# Revit family: IS_iLifeA_T4709_BIM_GB
name_source: partatom
category: Plumbing Fixtures
units: mm (PartAtom-declared; Revit-internal decimal feet)

## family parameters
Always vertical = No
Cut with Voids When Loaded = No
OmniClass Number = 23.45.05.14.14
OmniClass Title = Sinks/Lavatories
Part Type = Normal
Room Calculation Point = No
Round Connector Dimension = Use Diameter
Shared = No
Work Plane-Based = No

## types (1)
- T470901 - Ideal Standard i.life A  handrinse 35 cm with left hand taphole, white
    Accessories = https://www.idealstandard.co.uk
    AreaUnits = millimetres
    AssetType = fixed
    BIMObjectName = IS_IdealStandard_Wall-hunghandrinsebasins_i.lifeA_T4709
    BIMobject category = Wash Basins
    BIMobject category code = wash-basins
    BIMobject main category = Sanitary
    BIMobject main category code = sanitary
    BarCode = 8014140486862
    Brand = Ideal Standard
    Brand url = http://www.idealstandard.co.uk
    Color = White
    ConnectionType = Plumbing
    CurrencyUnit = £
    CurrentRevision = 1
    Date of publishing = 07/10/2022
    Description = Handrinse 35 cm with left Hand taphole, white
    DurationUnit = years
    Edition number = 1
    ElementType = fixed
    ExpectedLife = 99
    Features = Handrinse 35 cm with left Hand taphole, white
    Finish = White
    GTIN code = https://8014140486862
    Help = https://www.idealstandard.co.uk
    IFC Classification = Sanitary Terminal
    IfcExportAs = IfcSanitaryTerminalType
    IfcExportType = WASHHANDBASIN
    Installation instructions = https://www.idealstandard.co.uk
    InstallationDate = n /a
    InstallationInstructions = https://www.idealstandard.co.uk
    LinearUnits = millimetres
    MainColor = White
    MaintenanceInformation = https://www.idealstandard.co.uk
    Manufacturer = Ideal Standard
    Manufacturer name = Ideal Standard
    ManufacturerURL = https://www.idealstandard.co.uk
    Masterformat 2014 Code = 22 40 00
    Masterformat 2014 Description = Plumbing Fixtures
    Material = Ceramics
    Material main = Ceramics
    Model = T470901
    ModelNumber = T470901
    ModelReference = I.life A Handrinse 35 cm with left Hand taphole, white
    NBS Reference Code = 45-35-70/384
    NBS Reference Description = WC Pans
    Name = Wall-hunghandrinsebasins_i.lifeA_T4709_IdealStandard
    NettWeight = 7.6
    NominalDepth = 300 mm
    NominalHeight = 150 mm
    NominalWidth = 350 mm
    OmniClass Code = 23-31 19 00
    OmniClass Description = Toilets
    Product Guid = 4da78dc2-e301-44e8-831b-aff428082555
    Product SKU = T4709
    Product certification = https://www.idealstandard.co.uk
    Product data url = https://bimobject.com
    Product family = I.life A
    Product group = Basin
    Product name = IDEAL STANDARD I.LIFE A  HANDRINSE 35 CM WITH LEFT HAND TAPHOLE,
    Product url = https://www.idealstandard.co.uk
    ProductInformation = https://www.idealstandard.co.uk
    QR code = http://bimobject.com
    Shape = sculptured
    Size = 350 x 300 x 150 mm
    Space = Internal
    SpareParts = https://www.idealstandard.co.uk
    Technical description = https://www.idealstandard.co.uk
    UNSPSC Code = 301815
    URL = https://www.idealstandard.co.uk
    Uniclass 1.4 Code = L7212
    Uniclass 1.4 Description = Washbasins
    Uniclass 2.0 Code = Pr_40_30_79_95
    Uniclass 2.0 Description = Wall-Hung Hand Rinse Basins
    Uniclass 2015 Code = Pr_40_20_96_95
    Uniclass 2015 Name = Wall-hung hand rinse basins
    Uniclass2015Code = Pr_40_20_96_95
    Uniclass2015Title = Wall-hung hand rinse basins
    Uniclass2015Version = v1.27
    Uniformat II Code = D2010
    Uniformat II Description = Plumbing Fixtures
    Version = 1
    VolumeUnits = liters
    WRASURL = https://www.wrasapprovals.co.uk
    WarrantyDescription = manufacturer warranty
    WarrantyDurationUnit = years
    WashHandBasinMounting = Wall hung
    WashHandBasinType = Wall hung
    Weight Net (Kg) = 7.6
    Youtube clip = https://www.wrasapprovals.co.uk

## geometry (parser evidence)
native form markers: Sweep x2
no freeform markers — native parametric forms only
